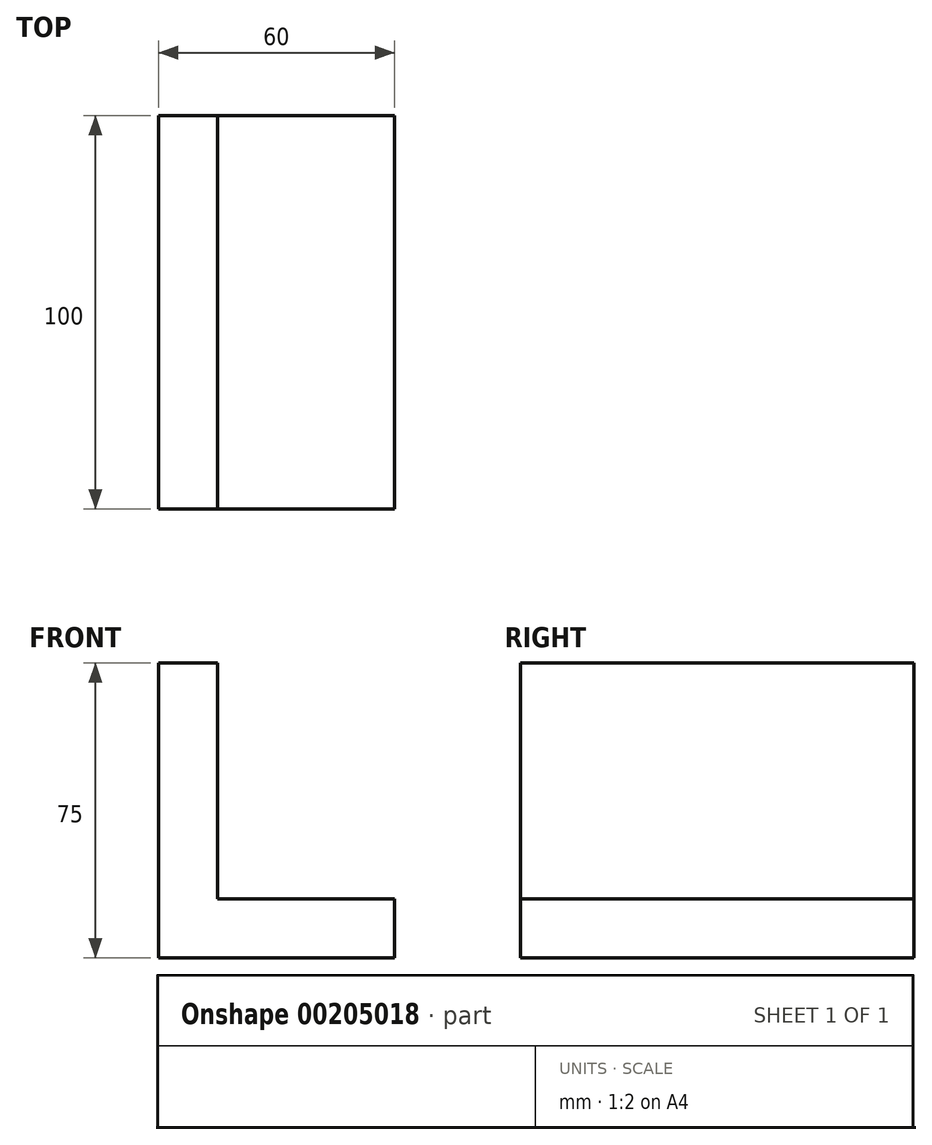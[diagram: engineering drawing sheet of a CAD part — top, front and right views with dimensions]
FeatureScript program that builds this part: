
annotation { "Feature Type Name" : "Feature", "Feature Type Description" : "" }
export const myFeature = defineFeature(function(context is Context, id is Id, definition is map)
    precondition{}
    {
        {
            var Q0;
            Q0=qCreatedBy(makeId("Front.planeOp"),FACE);
            var sketch = newSketch(context, id + "F0", { "sketchPlane" : qUnion([Q0])});
            skLineSegment(sketch, "E0", {"start": v(-15, 47.5) * mm, "end": v(-15, -27.5) * mm});
            skLineSegment(sketch, "E1", {"start": v(-15, -27.5) * mm, "end": v(45, -27.5) * mm});
            skLineSegment(sketch, "E2", {"start": v(45, -27.5) * mm, "end": v(45, -12.5) * mm});
            skLineSegment(sketch, "E3", {"start": v(-15, 47.5) * mm, "end": v(0, 47.5) * mm});
            skLineSegment(sketch, "E4", {"start": v(45, -12.5) * mm, "end": v(0, -12.5) * mm});
            skLineSegment(sketch, "E5", {"start": v(0, 47.5) * mm, "end": v(0, -12.5) * mm});
            skSolve(sketch);
        }
        {
            var Q0;
            Q0 = qSketchRegion(id + "F0", true);
            extrude(context, id + "F1", {"entities" : qUnion([Q0]), "depth" : 100 * mm});
        }
    });
